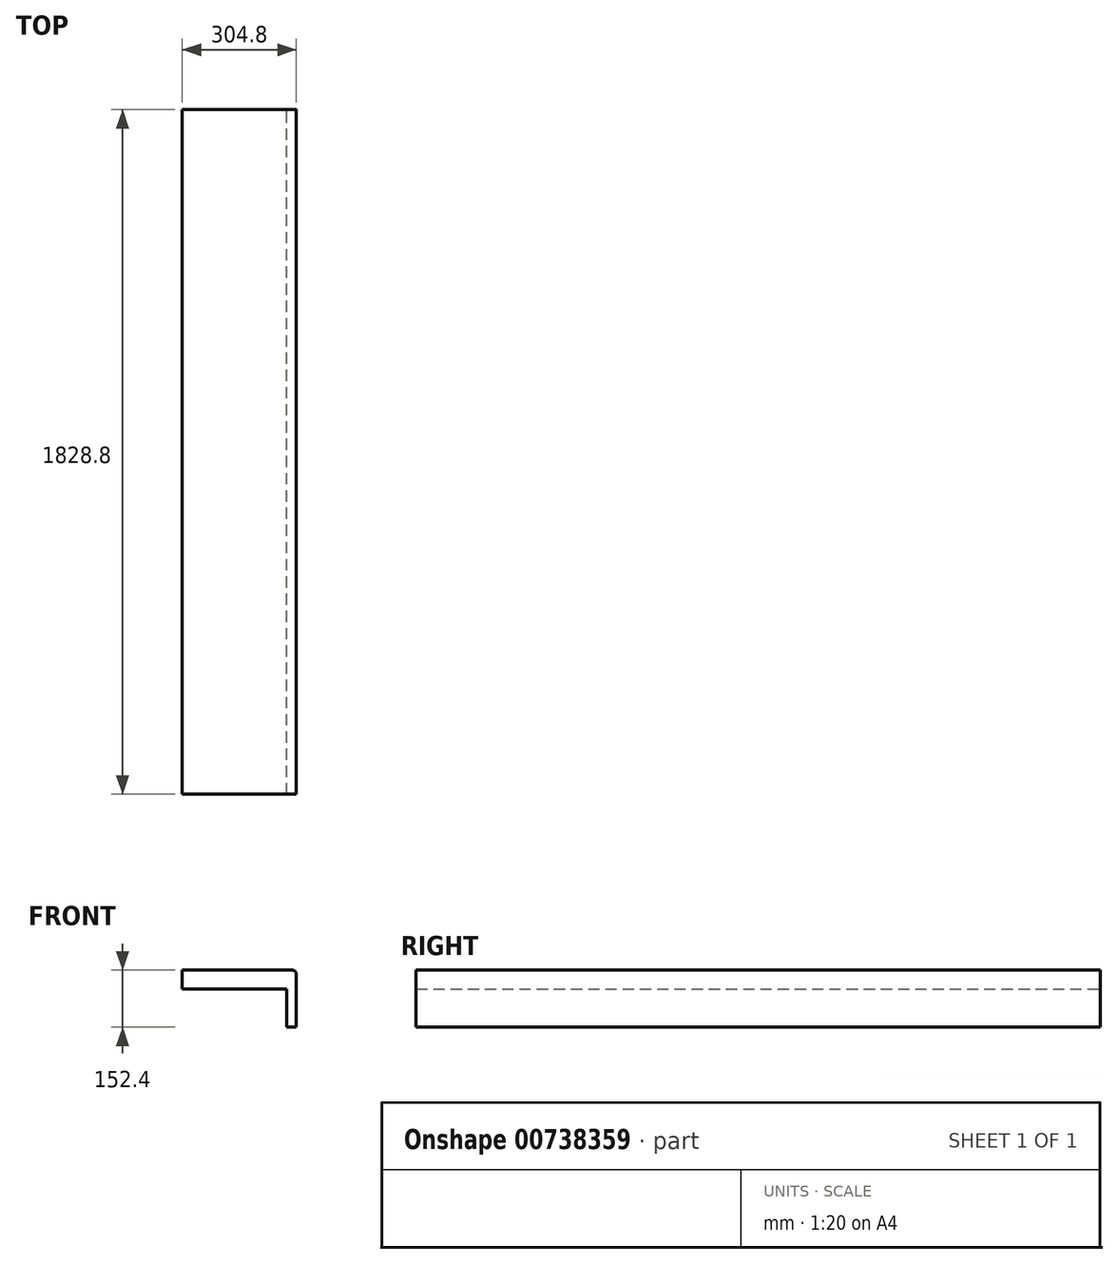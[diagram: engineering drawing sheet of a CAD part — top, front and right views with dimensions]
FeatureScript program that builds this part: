
annotation { "Feature Type Name" : "Feature", "Feature Type Description" : "" }
export const myFeature = defineFeature(function(context is Context, id is Id, definition is map)
    precondition{}
    {
        {
            var Q0;
            Q0=qCreatedBy(makeId("Front.planeOp"),FACE);
            var sketch = newSketch(context, id + "F0", { "sketchPlane" : qUnion([Q0])});
            skLineSegment(sketch, "E0", {"start": v(-96.7, 152.4) * mm, "end": v(-96.7, 101.6) * mm});
            skLineSegment(sketch, "E1", {"start": v(-96.7, 101.6) * mm, "end": v(182.7, 101.6) * mm});
            skLineSegment(sketch, "E2", {"start": v(182.7, 101.6) * mm, "end": v(182.7, 0) * mm});
            skLineSegment(sketch, "E3", {"start": v(208.1, 0) * mm, "end": v(182.7, 0) * mm});
            skLineSegment(sketch, "E4", {"start": v(-96.7, 152.4) * mm, "end": v(197, 152.4) * mm});
            skLineSegment(sketch, "E5", {"start": v(208.1, 141.29) * mm, "end": v(208.1, 0) * mm});
            skPoint(sketch, "E6.visualSharp", {"position": v(208.1, 152.4) * mm});
            skArc(sketch, "E6.filletArc", {"start": v(208.1, 141.29) * mm, "mid": v(204.85, 149.15) * mm, "end": v(197, 152.4) * mm});
            skSolve(sketch);
        }
        {
            var Q0;
            Q0=makeQuery(id+"F0.imprint","IMPRINT",FACE,{"disambiguationData":[TD([[makeQuery(id+"F0.imprint","IMPRINT",EDGE,{"derivedFrom":sQuery(id+"F0.wireOp",EDGE,"E0")}),1.0]])]});
            extrude(context, id + "F1", {"entities" : qUnion([Q0]), "depth" : 1828.8 * mm, "offsetDistance" : 25.4 * mm});
        }
    });
